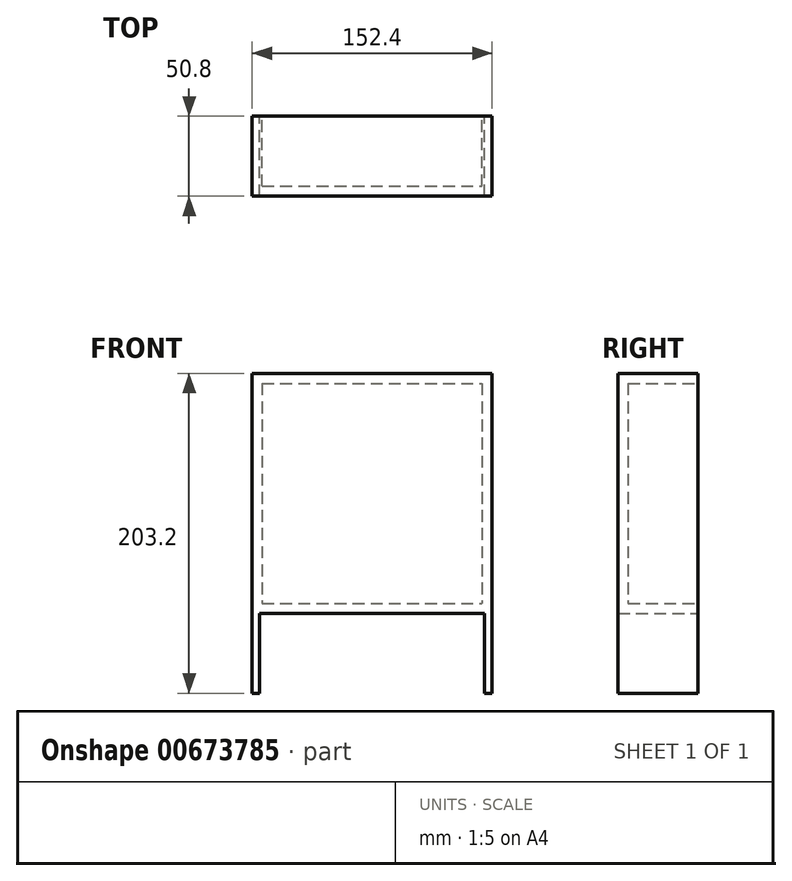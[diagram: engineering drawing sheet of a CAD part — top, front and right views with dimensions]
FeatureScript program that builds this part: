
annotation { "Feature Type Name" : "Feature", "Feature Type Description" : "" }
export const myFeature = defineFeature(function(context is Context, id is Id, definition is map)
    precondition{}
    {
        {
            var Q0;
            Q0=qCreatedBy(makeId("Front.planeOp"),FACE);
            var sketch = newSketch(context, id + "F0", { "sketchPlane" : qUnion([Q0])});
            skLineSegment(sketch, "E0.bottom", {"start": v(-76.2, 76.2) * mm, "end": v(76.2, 76.2) * mm});
            skLineSegment(sketch, "E0.top", {"start": v(-76.2, -76.2) * mm, "end": v(76.2, -76.2) * mm});
            skLineSegment(sketch, "E0.left", {"start": v(-76.2, 76.2) * mm, "end": v(-76.2, -76.2) * mm});
            skLineSegment(sketch, "E0.right", {"start": v(76.2, 76.2) * mm, "end": v(76.2, -76.2) * mm});
            skPoint(sketch, "E0.middle", {"position": v(0, 0) * mm});
            skSolve(sketch);
        }
        {
            var Q0;
            Q0 = qSketchRegion(id + "F0", true);
            extrude(context, id + "F1", {"entities" : qUnion([Q0]), "endBound" : BoundingType.SYMMETRIC, "depth" : 50.8 * mm, "offsetDistance" : 25.4 * mm});
        }
        {
            var Q0;
            Q0=makeQuery(id+"F1.opExtrude","CAP_FACE",FACE,{"disambiguationData":[OSD([sQuery(id+"F0.wireOp",EDGE,"E0.bottom"),sQuery(id+"F0.wireOp",EDGE,"E0.top"),sQuery(id+"F0.wireOp",EDGE,"E0.left"),sQuery(id+"F0.wireOp",EDGE,"E0.right")])],"isStart":true});
            var Q1;
            Q1=makeQuery(id+"F1.opExtrude","SWEPT_BODY",BODY,{"disambiguationData":[OSD([sQuery(id+"F0.wireOp",EDGE,"E0.bottom"),sQuery(id+"F0.wireOp",EDGE,"E0.top"),sQuery(id+"F0.wireOp",EDGE,"E0.left"),sQuery(id+"F0.wireOp",EDGE,"E0.right")])]});
            shell(context, id + "F2", {"entities" : qUnion([Q0]), "parts" : qUnion([Q1]), "thickness" : 6.35 * mm});
        }
        {
            var Q0;
            Q0=makeQuery(id+"F1.opExtrude","SWEPT_FACE",FACE,{"disambiguationData":[OSD([sQuery(id+"F0.wireOp",EDGE,"E0.top")])]});
            var sketch = newSketch(context, id + "F3", { "sketchPlane" : qUnion([Q0])});
            skLineSegment(sketch, "E1.bottom", {"start": v(-71.43, 25.4) * mm, "end": v(-76.2, 25.4) * mm});
            skLineSegment(sketch, "E1.top", {"start": v(-71.43, -25.4) * mm, "end": v(-76.2, -25.4) * mm});
            skLineSegment(sketch, "E1.left", {"start": v(-71.43, 25.4) * mm, "end": v(-71.43, -25.4) * mm});
            skLineSegment(sketch, "E1.right", {"start": v(-76.2, 25.4) * mm, "end": v(-76.2, -25.4) * mm});
            skLineSegment(sketch, "E2", {"start": v(0, 25.4) * mm, "end": v(0, -25.4) * mm, "construction": true});
            skLineSegment(sketch, "E3.MirrorCS", {"start": v(71.43, -25.4) * mm, "end": v(76.2, -25.4) * mm});
            skLineSegment(sketch, "E4.MirrorCS", {"start": v(71.43, 25.4) * mm, "end": v(76.2, 25.4) * mm});
            skLineSegment(sketch, "E5.MirrorCS", {"start": v(76.2, 25.4) * mm, "end": v(76.2, -25.4) * mm});
            skLineSegment(sketch, "E6.MirrorCS", {"start": v(71.43, 25.4) * mm, "end": v(71.43, -25.4) * mm});
            skSolve(sketch);
        }
        {
            var Q0;
            Q0=makeQuery(id+"F3.imprint","IMPRINT",FACE,{"disambiguationData":[TD([[makeQuery(id+"F3.imprint","IMPRINT",EDGE,{"derivedFrom":sQuery(id+"F3.wireOp",EDGE,"E1.bottom")}),-1.0]])]});
            var Q1;
            Q1=makeQuery(id+"F3.imprint","IMPRINT",FACE,{"disambiguationData":[TD([[makeQuery(id+"F3.imprint","IMPRINT",EDGE,{"derivedFrom":sQuery(id+"F3.wireOp",EDGE,"E3.MirrorCS")}),1.0]])]});
            extrude(context, id + "F4", {"entities" : qUnion([Q0, Q1]), "operationType" : NewBodyOperationType.ADD, "depth" : 50.8 * mm, "offsetDistance" : 25.4 * mm});
        }
    });
